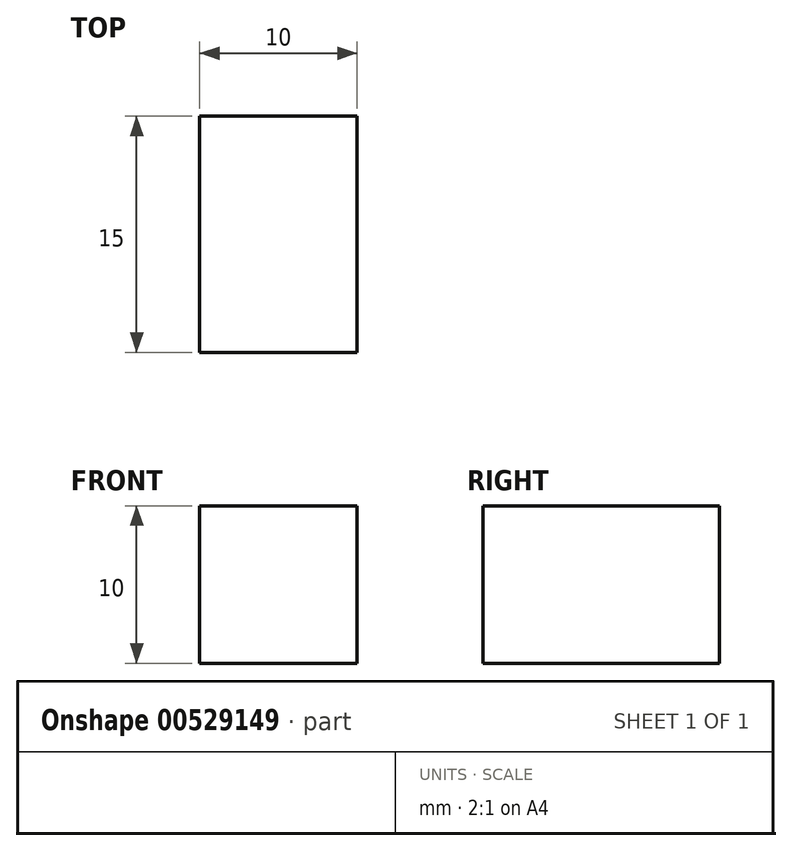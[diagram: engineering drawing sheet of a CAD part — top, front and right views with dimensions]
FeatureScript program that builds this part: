
annotation { "Feature Type Name" : "Feature", "Feature Type Description" : "" }
export const myFeature = defineFeature(function(context is Context, id is Id, definition is map)
    precondition{}
    {
        {
            var Q0;
            Q0=qCreatedBy(makeId("Right.planeOp"),FACE);
            var sketch = newSketch(context, id + "F0", { "sketchPlane" : qUnion([Q0])});
            skLineSegment(sketch, "E0.bottom", {"start": v(7.5, -5) * mm, "end": v(-7.5, -5) * mm});
            skLineSegment(sketch, "E0.top", {"start": v(7.5, 5) * mm, "end": v(-7.5, 5) * mm});
            skLineSegment(sketch, "E0.left", {"start": v(7.5, -5) * mm, "end": v(7.5, 5) * mm});
            skLineSegment(sketch, "E0.right", {"start": v(-7.5, -5) * mm, "end": v(-7.5, 5) * mm});
            skPoint(sketch, "E0.middle", {"position": v(0, 0) * mm});
            skSolve(sketch);
        }
        {
            var Q0;
            Q0=makeQuery(id+"F0.imprint","IMPRINT",FACE,{"disambiguationData":[TD([[makeQuery(id+"F0.imprint","IMPRINT",EDGE,{"derivedFrom":sQuery(id+"F0.wireOp",EDGE,"E0.bottom")}),-1.0]])]});
            extrude(context, id + "F1", {"entities" : qUnion([Q0]), "depth" : 10 * mm, "offsetDistance" : 25 * mm});
        }
    });
